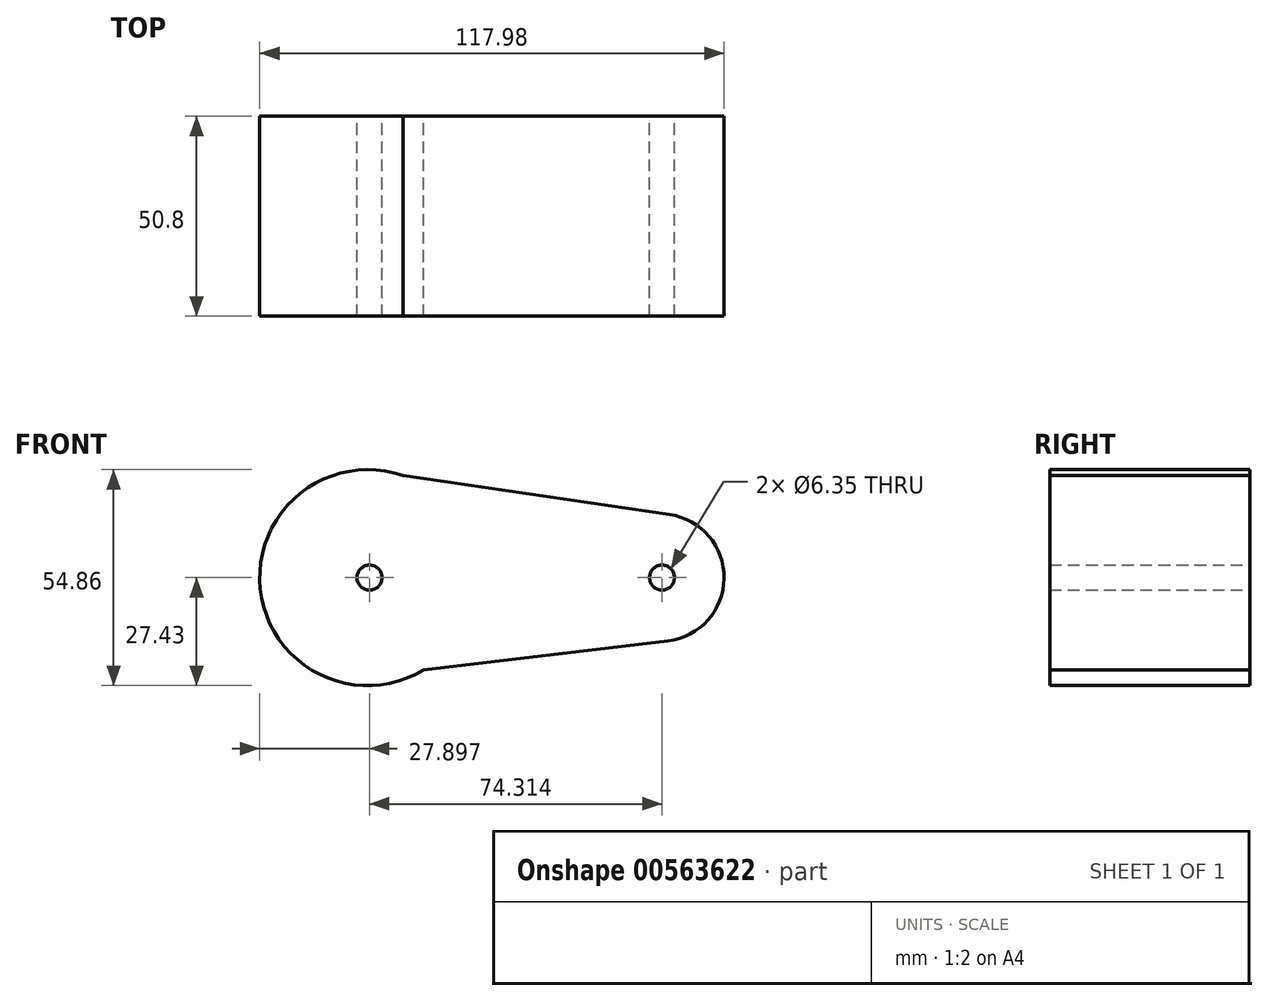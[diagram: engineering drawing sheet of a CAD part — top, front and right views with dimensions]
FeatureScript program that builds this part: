
annotation { "Feature Type Name" : "Feature", "Feature Type Description" : "" }
export const myFeature = defineFeature(function(context is Context, id is Id, definition is map)
    precondition{}
    {
        {
            var Q0;
            Q0=qCreatedBy(makeId("Front.planeOp"),FACE);
            var sketch = newSketch(context, id + "F0", { "sketchPlane" : qUnion([Q0])});
            skCircle(sketch, "E0", {"center": v(-35.32, 0) * mm, "radius": 27.43 * mm});
            skCircle(sketch, "E1", {"center": v(39.04, 0) * mm, "radius": 16.18 * mm});
            skLineSegment(sketch, "E2", {"start": v(-26.38, 25.93) * mm, "end": v(41.39, 16.01) * mm});
            skLineSegment(sketch, "E3", {"start": v(-21.13, -23.47) * mm, "end": v(40.96, -16.07) * mm});
            skSolve(sketch);
        }
        {
            var Q0;
            Q0=qCreatedBy(makeId("Front.planeOp"),FACE);
            var sketch = newSketch(context, id + "F1", { "sketchPlane" : qUnion([Q0])});
            skCircle(sketch, "E4", {"center": v(-34.85, 0) * mm, "radius": 16.99 * mm});
            skCircle(sketch, "E5", {"center": v(39.46, 0) * mm, "radius": 10.38 * mm});
            skSolve(sketch);
        }
        {
            var Q0;
            {var subQ0=sQuery(id+"F0.wireOp",EDGE,"E0");var subQ1=makeQuery(id+"F0.imprint","INTERSECT",VERTEX,{"derivedFrom":[subQ0,sQuery(id+"F0.wireOp",EDGE,"E2")]});Q0=makeQuery(id+"F0.imprint","IMPRINT",FACE,{"disambiguationData":[TD([[makeQuery(id+"F0.imprint","IMPRINT",EDGE,{"disambiguationData":[TD([[subQ1,-1.0]])],"derivedFrom":subQ0}),1.0]])]});}
            var Q1;
            {var subQ0=sQuery(id+"F0.wireOp",EDGE,"E2");Q1=makeQuery(id+"F0.imprint","IMPRINT",FACE,{"disambiguationData":[TD([[makeQuery(id+"F0.imprint","IMPRINT",EDGE,{"derivedFrom":subQ0}),-1.0]])]});}
            var Q2;
            {var subQ0=sQuery(id+"F0.wireOp",EDGE,"E1");var subQ1=makeQuery(id+"F0.imprint","INTERSECT",VERTEX,{"derivedFrom":[subQ0,sQuery(id+"F0.wireOp",EDGE,"E2")]});Q2=makeQuery(id+"F0.imprint","IMPRINT",FACE,{"disambiguationData":[TD([[makeQuery(id+"F0.imprint","IMPRINT",EDGE,{"disambiguationData":[TD([[subQ1,-1.0]])],"derivedFrom":subQ0}),1.0]])]});}
            extrude(context, id + "F2", {"entities" : qUnion([Q0, Q1, Q2]), "depth" : 50.8 * mm, "offsetDistance" : 25.4 * mm});
        }
        {
            var Q0;
            Q0=sQuery(id+"F1.wireOp",VERTEX,"E4.center");
            var Q1;
            Q1=sQuery(id+"F1.wireOp",VERTEX,"E5.center");
            var Q2;
            Q2=makeQuery(id+"F2.opExtrude","SWEPT_BODY",BODY,{"disambiguationData":[OSD([sQuery(id+"F0.wireOp",EDGE,"E0"),sQuery(id+"F0.wireOp",EDGE,"E1"),sQuery(id+"F0.wireOp",EDGE,"E2"),sQuery(id+"F0.wireOp",EDGE,"E3")])]});
            hole(context, id + "F3", {"style" : HoleStyle.SIMPLE, "endStyle" : HoleEndStyle.THROUGH, "oppositeDirection" : true, "holeDiameter" : 6.35 * mm, "majorDiameter" : 6.35 * mm, "isTappedThrough" : true, "tappedDepth" : 12.7 * mm, "tapClearance" : 3, "locations" : qUnion([Q0, Q1]), "scope" : qUnion([Q2])});
        }
    });
